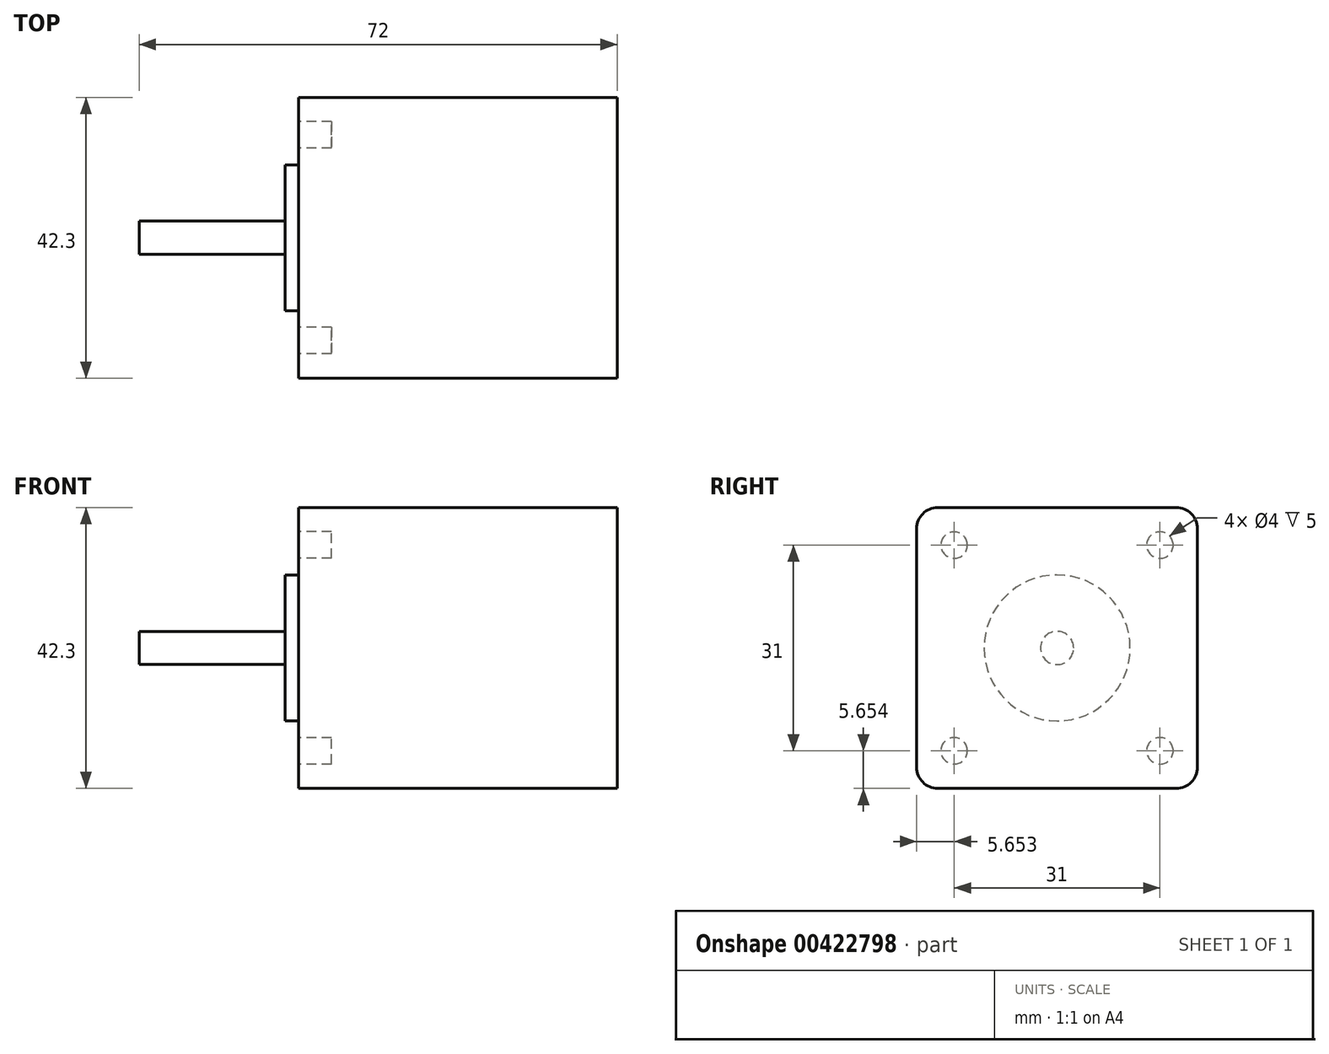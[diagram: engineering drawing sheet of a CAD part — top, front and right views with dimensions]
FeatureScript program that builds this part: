
annotation { "Feature Type Name" : "Feature", "Feature Type Description" : "" }
export const myFeature = defineFeature(function(context is Context, id is Id, definition is map)
    precondition{}
    {
        {
            var Q0;
            Q0=qCreatedBy(makeId("Right.planeOp"),FACE);
            var sketch = newSketch(context, id + "F0", { "sketchPlane" : qUnion([Q0])});
            skLineSegment(sketch, "E0.bottom", {"start": v(-8.43, 2.1) * mm, "end": v(27.52, 2.1) * mm});
            skLineSegment(sketch, "E0.top", {"start": v(-8.43, -40.2) * mm, "end": v(27.52, -40.2) * mm});
            skLineSegment(sketch, "E0.left", {"start": v(-11.6, -1.07) * mm, "end": v(-11.6, -37.02) * mm});
            skLineSegment(sketch, "E0.right", {"start": v(30.7, -1.07) * mm, "end": v(30.7, -37.02) * mm});
            skCircle(sketch, "E1", {"center": v(9.54, -19.05) * mm, "radius": 2.5 * mm});
            skCircle(sketch, "E2", {"center": v(9.54, -19.05) * mm, "radius": 11 * mm});
            skLineSegment(sketch, "E3", {"start": v(9.54, 2.1) * mm, "end": v(9.54, -40.2) * mm, "construction": true});
            skLineSegment(sketch, "E4", {"start": v(-11.6, -19.05) * mm, "end": v(30.7, -19.05) * mm, "construction": true});
            skPoint(sketch, "E5.visualSharp", {"position": v(-11.6, 2.1) * mm});
            skArc(sketch, "E5.filletArc", {"start": v(-8.43, 2.1) * mm, "mid": v(-10.68, 1.17) * mm, "end": v(-11.6, -1.07) * mm});
            skPoint(sketch, "E6.visualSharp", {"position": v(30.7, 2.1) * mm});
            skArc(sketch, "E6.filletArc", {"start": v(30.7, -1.07) * mm, "mid": v(29.76, 1.17) * mm, "end": v(27.52, 2.1) * mm});
            skPoint(sketch, "E7.visualSharp", {"position": v(30.7, -40.2) * mm});
            skArc(sketch, "E7.filletArc", {"start": v(27.52, -40.2) * mm, "mid": v(29.76, -39.27) * mm, "end": v(30.7, -37.02) * mm});
            skPoint(sketch, "E8.visualSharp", {"position": v(-11.6, -40.2) * mm});
            skArc(sketch, "E8.filletArc", {"start": v(-11.6, -37.02) * mm, "mid": v(-10.68, -39.27) * mm, "end": v(-8.43, -40.2) * mm});
            skSolve(sketch);
        }
        {
            var Q0;
            Q0=makeQuery(id+"F0.imprint","IMPRINT",FACE,{"disambiguationData":[TD([[makeQuery(id+"F0.imprint","IMPRINT",EDGE,{"derivedFrom":sQuery(id+"F0.wireOp",EDGE,"E0.bottom")}),-1.0]])]});
            var Q1;
            Q1=makeQuery(id+"F0.imprint","IMPRINT",FACE,{"disambiguationData":[TD([[makeQuery(id+"F0.imprint","IMPRINT",EDGE,{"derivedFrom":sQuery(id+"F0.wireOp",EDGE,"E1")}),-1.0]])]});
            var Q2;
            Q2=makeQuery(id+"F0.imprint","IMPRINT",FACE,{"disambiguationData":[TD([[makeQuery(id+"F0.imprint","IMPRINT",EDGE,{"derivedFrom":sQuery(id+"F0.wireOp",EDGE,"E1")}),1.0]])]});
            extrude(context, id + "F1", {"entities" : qUnion([Q0, Q1, Q2]), "depth" : 48 * mm});
        }
        {
            var Q0;
            Q0=makeQuery(id+"F0.imprint","IMPRINT",FACE,{"disambiguationData":[TD([[makeQuery(id+"F0.imprint","IMPRINT",EDGE,{"derivedFrom":sQuery(id+"F0.wireOp",EDGE,"E1")}),-1.0]])]});
            var Q1;
            Q1=makeQuery(id+"F0.imprint","IMPRINT",FACE,{"disambiguationData":[TD([[makeQuery(id+"F0.imprint","IMPRINT",EDGE,{"derivedFrom":sQuery(id+"F0.wireOp",EDGE,"E1")}),1.0]])]});
            extrude(context, id + "F2", {"entities" : qUnion([Q0, Q1]), "operationType" : NewBodyOperationType.ADD, "oppositeDirection" : true, "depth" : 2 * mm});
        }
        {
            var Q0;
            Q0=makeQuery(id+"F0.imprint","IMPRINT",FACE,{"disambiguationData":[TD([[makeQuery(id+"F0.imprint","IMPRINT",EDGE,{"derivedFrom":sQuery(id+"F0.wireOp",EDGE,"E1")}),1.0]])]});
            extrude(context, id + "F3", {"entities" : qUnion([Q0]), "operationType" : NewBodyOperationType.ADD, "oppositeDirection" : true, "depth" : 24 * mm});
        }
        {
            var Q0;
            Q0=makeQuery(id+"F0.imprint","IMPRINT",FACE,{"disambiguationData":[TD([[makeQuery(id+"F0.imprint","IMPRINT",EDGE,{"derivedFrom":sQuery(id+"F0.wireOp",EDGE,"E0.bottom")}),-1.0]])]});
            var sketch = newSketch(context, id + "F4", { "sketchPlane" : qUnion([Q0])});
            skCircle(sketch, "E9", {"center": v(25.04, -3.55) * mm, "radius": 2 * mm});
            skLineSegment(sketch, "E10", {"start": v(25.04, -3.55) * mm, "end": v(-5.96, -3.55) * mm});
            skCircle(sketch, "E11", {"center": v(-5.96, -3.55) * mm, "radius": 2 * mm});
            skPoint(sketch, "E12", {"position": v(9.54, -3.55) * mm});
            skLineSegment(sketch, "E13", {"start": v(25.04, -3.55) * mm, "end": v(25.04, -34.55) * mm});
            skLineSegment(sketch, "E14", {"start": v(25.04, -34.55) * mm, "end": v(-5.96, -34.55) * mm});
            skCircle(sketch, "E15", {"center": v(25.04, -34.55) * mm, "radius": 2 * mm});
            skCircle(sketch, "E16", {"center": v(-5.96, -34.55) * mm, "radius": 2 * mm});
            skPoint(sketch, "E17", {"position": v(9.54, -34.55) * mm});
            skLineSegment(sketch, "E18", {"start": v(9.54, -3.55) * mm, "end": v(9.54, -34.55) * mm, "construction": true});
            skPoint(sketch, "E19", {"position": v(9.54, -19.05) * mm});
            skSolve(sketch);
        }
        {
            var Q0;
            {var subQ0=sQuery(id+"F4.wireOp",EDGE,"E10");var subQ1=sQuery(id+"F4.wireOp",EDGE,"E9");var subQ2=makeQuery(id+"F4.imprint","INTERSECT",VERTEX,{"derivedFrom":[subQ1,subQ0]});Q0=makeQuery(id+"F4.imprint","IMPRINT",FACE,{"disambiguationData":[TD([[makeQuery(id+"F4.imprint","IMPRINT",EDGE,{"disambiguationData":[TD([[subQ2,-1.0]])],"derivedFrom":subQ1}),1.0]])]});}
            var Q1;
            {var subQ0=sQuery(id+"F4.wireOp",EDGE,"E10");var subQ1=sQuery(id+"F4.wireOp",EDGE,"E9");var subQ2=makeQuery(id+"F4.imprint","INTERSECT",VERTEX,{"derivedFrom":[subQ1,subQ0]});Q1=makeQuery(id+"F4.imprint","IMPRINT",FACE,{"disambiguationData":[TD([[makeQuery(id+"F4.imprint","IMPRINT",EDGE,{"disambiguationData":[TD([[subQ2,1.0]])],"derivedFrom":subQ1}),1.0]])]});}
            var Q2;
            {var subQ0=sQuery(id+"F4.wireOp",EDGE,"E14");var subQ1=sQuery(id+"F4.wireOp",EDGE,"E13");var subQ2=makeQuery(id+"F4.imprint","INTERSECT",VERTEX,{"derivedFrom":[subQ1,subQ0]});Q2=makeQuery(id+"F4.imprint","IMPRINT",FACE,{"disambiguationData":[TD([[makeQuery(id+"F4.imprint","IMPRINT",EDGE,{"disambiguationData":[TD([[subQ2,1.0]])],"derivedFrom":subQ1}),1.0]])]});}
            var Q3;
            {var subQ0=sQuery(id+"F4.wireOp",EDGE,"E14");var subQ1=sQuery(id+"F4.wireOp",EDGE,"E13");var subQ2=makeQuery(id+"F4.imprint","INTERSECT",VERTEX,{"derivedFrom":[subQ1,subQ0]});Q3=makeQuery(id+"F4.imprint","IMPRINT",FACE,{"disambiguationData":[TD([[makeQuery(id+"F4.imprint","IMPRINT",EDGE,{"disambiguationData":[TD([[subQ2,1.0]])],"derivedFrom":subQ1}),-1.0]])]});}
            var Q4;
            Q4=makeQuery(id+"F4.imprint","IMPRINT",FACE,{"disambiguationData":[TD([[makeQuery(id+"F4.imprint","IMPRINT",EDGE,{"derivedFrom":sQuery(id+"F4.wireOp",EDGE,"E16")}),1.0]])]});
            var Q5;
            Q5=makeQuery(id+"F4.imprint","IMPRINT",FACE,{"disambiguationData":[TD([[makeQuery(id+"F4.imprint","IMPRINT",EDGE,{"derivedFrom":sQuery(id+"F4.wireOp",EDGE,"E11")}),1.0]])]});
            extrude(context, id + "F5", {"entities" : qUnion([Q0, Q1, Q2, Q3, Q4, Q5]), "operationType" : NewBodyOperationType.REMOVE, "depth" : 5 * mm});
        }
    });
